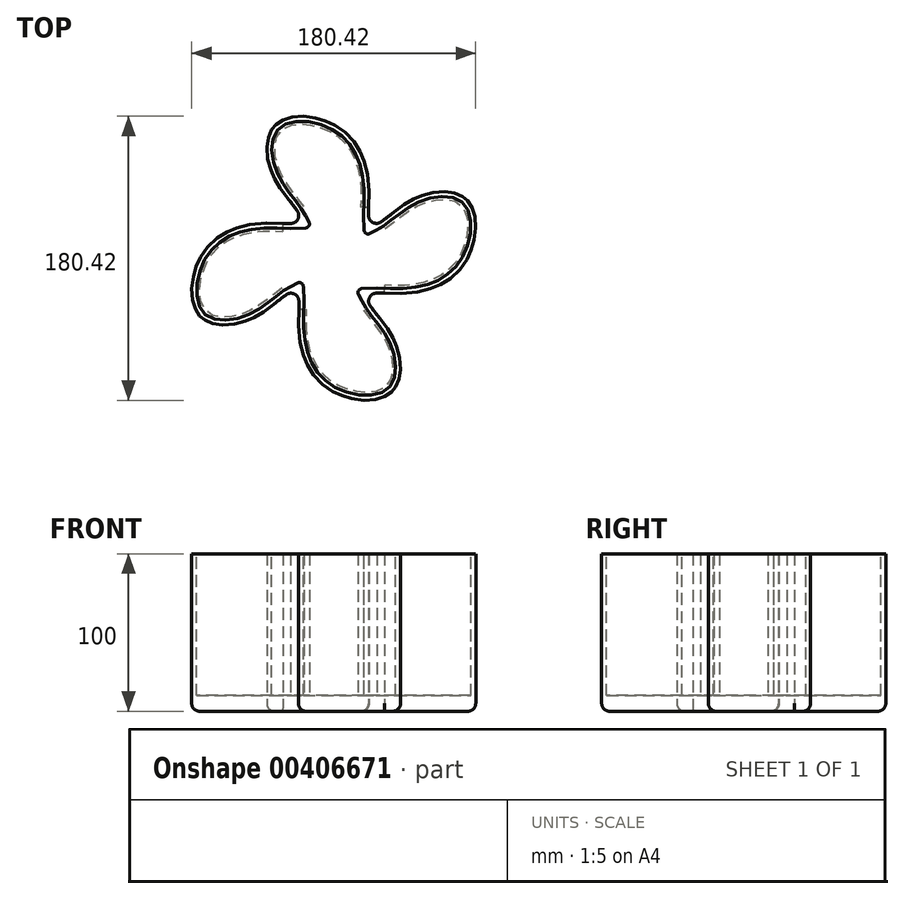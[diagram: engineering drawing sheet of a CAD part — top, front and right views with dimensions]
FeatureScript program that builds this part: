
annotation { "Feature Type Name" : "Feature", "Feature Type Description" : "" }
export const myFeature = defineFeature(function(context is Context, id is Id, definition is map)
    precondition{}
    {
        {
            var Q0;
            Q0=qCreatedBy(makeId("Top.planeOp"),FACE);
            var sketch = newSketch(context, id + "F0", { "sketchPlane" : qUnion([Q0])});
            skCircle(sketch, "E0", {"center": v(0, 0) * mm, "radius": 33.27 * mm, "construction": true});
            skFitSpline(sketch, "E1", {"points": [v(18.8, 27.45) * mm, v(15.3, 63.44) * mm, v(-5.91, 84.24) * mm, v(-35.04, 82.4) * mm, v(-36.55, 55.7) * mm, v(-21.57, 33.09) * mm, v(-14.6, 20.56) * mm], "startDerivative": vector(13.96, 201.86) * mm, "endDerivative": vector(40.78, -91.22) * mm});
            skLineSegment(sketch, "E2", {"start": v(-14.6, 20.56) * mm, "end": v(18.8, 27.45) * mm});
            skFitSpline(sketch, "E3.0", {"points": [v(21.79, 27.24) * mm, v(22.08, 31.5) * mm, v(22.45, 39.97) * mm, v(21.83, 50.18) * mm, v(20.34, 57.95) * mm, v(18.9, 62.61) * mm, v(17.41, 66.19) * mm, v(15.7, 69.63) * mm, v(13.11, 73.69) * mm, v(9.34, 78.06) * mm, v(4.92, 81.88) * mm, v(0.7, 84.54) * mm, v(-2.96, 86.31) * mm, v(-5.86, 87.46) * mm, v(-8.89, 88.42) * mm, v(-13.03, 89.42) * mm, v(-18.32, 90.14) * mm, v(-23.53, 90.07) * mm, v(-27.5, 89.45) * mm, v(-30.35, 88.67) * mm, v(-33.03, 87.56) * mm, v(-35.08, 86.3) * mm, v(-36.57, 85.1) * mm, v(-37.6, 84.08) * mm, v(-38.53, 82.98) * mm, v(-39.6, 81.4) * mm, v(-40.68, 79.29) * mm, v(-41.58, 76.57) * mm, v(-42.13, 73.73) * mm, v(-42.45, 69.8) * mm, v(-42.16, 64.76) * mm, v(-41.1, 59.74) * mm, v(-39.85, 55.86) * mm, v(-38.73, 53.05) * mm, v(-37.46, 50.4) * mm, v(-35.6, 47.05) * mm, v(-33.07, 43.18) * mm, v(-29.91, 38.98) * mm, v(-27.37, 35.78) * mm, v(-25.5, 33.38) * mm, v(-24.43, 31.95) * mm, v(-23.65, 30.83) * mm, v(-22.9, 29.73) * mm, v(-22.02, 28.37) * mm, v(-21.07, 26.78) * mm, v(-19.9, 24.7) * mm, v(-18.64, 22.19) * mm, v(-17.76, 20.27) * mm, v(-17.35, 19.33) * mm]});
            skLineSegment(sketch, "E4", {"start": v(-17.35, 19.33) * mm, "end": v(-14.6, 20.56) * mm});
            skLineSegment(sketch, "E5", {"start": v(18.8, 27.45) * mm, "end": v(22.14, 33.67) * mm});
            skLineSegment(sketch, "E6", {"start": v(22.14, 33.67) * mm, "end": v(22.14, 17.35) * mm});
            skLineSegment(sketch, "E7", {"start": v(22.14, 17.35) * mm, "end": v(19.33, 17.35) * mm});
            skLineSegment(sketch, "E8", {"start": v(19.33, 17.35) * mm, "end": v(18.8, 27.45) * mm});
            skPoint(sketch, "E9", {"position": v(0.24, 81.24) * mm});
            skSolve(sketch);
        }
        {
            var Q0;
            Q0=makeQuery(id+"F0.imprint","IMPRINT",FACE,{"disambiguationData":[TD([[makeQuery(id+"F0.imprint","IMPRINT",EDGE,{"derivedFrom":sQuery(id+"F0.wireOp",EDGE,"E1")}),-1.0]])]});
            var Q1;
            Q1=makeQuery(id+"F0.imprint","IMPRINT",FACE,{"disambiguationData":[TD([[makeQuery(id+"F0.imprint","IMPRINT",EDGE,{"derivedFrom":sQuery(id+"F0.wireOp",EDGE,"E5")}),-1.0]])]});
            extrude(context, id + "F1", {"entities" : qUnion([Q0, Q1]), "depth" : 100 * mm});
        }
        {
            var Q0;
            Q0=makeQuery(id+"F1.opExtrude","SWEPT_BODY",BODY,{"disambiguationData":[OSD([sQuery(id+"F0.wireOp",EDGE,"E1"),sQuery(id+"F0.wireOp",EDGE,"E3.0"),sQuery(id+"F0.wireOp",EDGE,"E4"),sQuery(id+"F0.wireOp",EDGE,"E5")])]});
            var Q1;
            Q1=sQuery(id+"F0.wireOp",EDGE,"E0");
            circularPattern(context, id + "F2", {"entities" : qUnion([Q0]), "axis" : qUnion([Q1]), "angle" : 360 * degree, "instanceCount" : 4, "equalSpace" : true});
        }
        {
            var Q0;
            Q0=makeQuery(id+"F1.opExtrude","SWEPT_BODY",BODY,{"disambiguationData":[OSD([sQuery(id+"F0.wireOp",EDGE,"E1"),sQuery(id+"F0.wireOp",EDGE,"E3.0"),sQuery(id+"F0.wireOp",EDGE,"E4"),sQuery(id+"F0.wireOp",EDGE,"E6"),sQuery(id+"F0.wireOp",EDGE,"E7"),sQuery(id+"F0.wireOp",EDGE,"E8")])]});
            var Q1;
            Q1=makeQuery(id+"F2.opPattern","COPY",BODY,{"derivedFrom":makeQuery(id+"F1.opExtrude","SWEPT_BODY",BODY,{"disambiguationData":[OSD([sQuery(id+"F0.wireOp",EDGE,"E1"),sQuery(id+"F0.wireOp",EDGE,"E3.0"),sQuery(id+"F0.wireOp",EDGE,"E4"),sQuery(id+"F0.wireOp",EDGE,"E6"),sQuery(id+"F0.wireOp",EDGE,"E7"),sQuery(id+"F0.wireOp",EDGE,"E8")])]}),"instanceName":"1"});
            var Q2;
            Q2=makeQuery(id+"F2.opPattern","COPY",BODY,{"derivedFrom":makeQuery(id+"F1.opExtrude","SWEPT_BODY",BODY,{"disambiguationData":[OSD([sQuery(id+"F0.wireOp",EDGE,"E1"),sQuery(id+"F0.wireOp",EDGE,"E3.0"),sQuery(id+"F0.wireOp",EDGE,"E4"),sQuery(id+"F0.wireOp",EDGE,"E6"),sQuery(id+"F0.wireOp",EDGE,"E7"),sQuery(id+"F0.wireOp",EDGE,"E8")])]}),"instanceName":"3"});
            booleanBodies(context, id + "F3", {"operationType" : BooleanOperationType.UNION, "tools" : qUnion([Q0, Q1, Q2])});
        }
        {
            var Q0;
            Q0=makeQuery(id+"F1.opExtrude","SWEPT_BODY",BODY,{"disambiguationData":[OSD([sQuery(id+"F0.wireOp",EDGE,"E1"),sQuery(id+"F0.wireOp",EDGE,"E3.0"),sQuery(id+"F0.wireOp",EDGE,"E4"),sQuery(id+"F0.wireOp",EDGE,"E6"),sQuery(id+"F0.wireOp",EDGE,"E7"),sQuery(id+"F0.wireOp",EDGE,"E8")])]});
            var Q1;
            Q1=makeQuery(id+"F2.opPattern","COPY",BODY,{"derivedFrom":makeQuery(id+"F1.opExtrude","SWEPT_BODY",BODY,{"disambiguationData":[OSD([sQuery(id+"F0.wireOp",EDGE,"E1"),sQuery(id+"F0.wireOp",EDGE,"E3.0"),sQuery(id+"F0.wireOp",EDGE,"E4"),sQuery(id+"F0.wireOp",EDGE,"E6"),sQuery(id+"F0.wireOp",EDGE,"E7"),sQuery(id+"F0.wireOp",EDGE,"E8")])]}),"instanceName":"2"});
            booleanBodies(context, id + "F4", {"operationType" : BooleanOperationType.UNION, "tools" : qUnion([Q0, Q1])});
        }
        {
            var Q0;
            Q0=makeQuery(id+"F4.opBoolean","INTERSECT",EDGE,{"derivedFrom":[makeQuery(id+"F2.opPattern","COPY",FACE,{"derivedFrom":makeQuery(id+"F1.opExtrude","SWEPT_FACE",FACE,{"disambiguationData":[OSD([sQuery(id+"F0.wireOp",EDGE,"E3.0")])]}),"instanceName":"1"}),makeQuery(id+"F2.opPattern","COPY",FACE,{"derivedFrom":makeQuery(id+"F1.opExtrude","SWEPT_FACE",FACE,{"disambiguationData":[OSD([sQuery(id+"F0.wireOp",EDGE,"E6")])]}),"instanceName":"2"})]});
            var Q1;
            Q1=makeQuery(id+"F4.opBoolean","INTERSECT",EDGE,{"derivedFrom":[makeQuery(id+"F2.opPattern","COPY",FACE,{"derivedFrom":makeQuery(id+"F1.opExtrude","SWEPT_FACE",FACE,{"disambiguationData":[OSD([sQuery(id+"F0.wireOp",EDGE,"E3.0")])]}),"instanceName":"2"}),makeQuery(id+"F2.opPattern","COPY",FACE,{"derivedFrom":makeQuery(id+"F1.opExtrude","SWEPT_FACE",FACE,{"disambiguationData":[OSD([sQuery(id+"F0.wireOp",EDGE,"E6")])]}),"instanceName":"3"})]});
            var Q2;
            Q2=makeQuery(id+"F3.opBoolean","INTERSECT",EDGE,{"derivedFrom":[makeQuery(id+"F1.opExtrude","SWEPT_FACE",FACE,{"disambiguationData":[OSD([sQuery(id+"F0.wireOp",EDGE,"E3.0")])]}),makeQuery(id+"F2.opPattern","COPY",FACE,{"derivedFrom":makeQuery(id+"F1.opExtrude","SWEPT_FACE",FACE,{"disambiguationData":[OSD([sQuery(id+"F0.wireOp",EDGE,"E6")])]}),"instanceName":"1"})]});
            var Q3;
            Q3=makeQuery(id+"F3.opBoolean","INTERSECT",EDGE,{"derivedFrom":[makeQuery(id+"F1.opExtrude","SWEPT_FACE",FACE,{"disambiguationData":[OSD([sQuery(id+"F0.wireOp",EDGE,"E6")])]}),makeQuery(id+"F2.opPattern","COPY",FACE,{"derivedFrom":makeQuery(id+"F1.opExtrude","SWEPT_FACE",FACE,{"disambiguationData":[OSD([sQuery(id+"F0.wireOp",EDGE,"E3.0")])]}),"instanceName":"3"})]});
            fillet(context, id + "F5", {"entities" : qUnion([Q0, Q1, Q2, Q3]), "radius" : 5 * mm, "tangentPropagation" : true, "allowEdgeOverflow" : false});
        }
        {
            var Q0;
            Q0=makeQuery(id+"F2.opPattern","COPY",EDGE,{"derivedFrom":makeQuery(id+"F1.opExtrude","SWEPT_EDGE",EDGE,{"disambiguationData":[OSD([sQuery(id+"F0.wireOp",EDGE,"E1"),sQuery(id+"F0.wireOp",EDGE,"E2"),sQuery(id+"F0.wireOp",EDGE,"E4")])]}),"instanceName":"2"});
            var Q1;
            Q1=makeQuery(id+"F4.opBoolean","INTERSECT",EDGE,{"derivedFrom":[makeQuery(id+"F2.opPattern","COPY",FACE,{"derivedFrom":makeQuery(id+"F1.opExtrude","SWEPT_FACE",FACE,{"disambiguationData":[OSD([sQuery(id+"F0.wireOp",EDGE,"E3.0")])]}),"instanceName":"2"}),makeQuery(id+"F2.opPattern","COPY",FACE,{"derivedFrom":makeQuery(id+"F1.opExtrude","SWEPT_FACE",FACE,{"disambiguationData":[OSD([sQuery(id+"F0.wireOp",EDGE,"E8")])]}),"instanceName":"3"})]});
            var Q2;
            Q2=makeQuery(id+"F2.opPattern","COPY",EDGE,{"derivedFrom":makeQuery(id+"F1.opExtrude","SWEPT_EDGE",EDGE,{"disambiguationData":[OSD([sQuery(id+"F0.wireOp",EDGE,"E1"),sQuery(id+"F0.wireOp",EDGE,"E2"),sQuery(id+"F0.wireOp",EDGE,"E4")])]}),"instanceName":"3"});
            var Q3;
            Q3=makeQuery(id+"F3.opBoolean","INTERSECT",EDGE,{"derivedFrom":[makeQuery(id+"F1.opExtrude","SWEPT_FACE",FACE,{"disambiguationData":[OSD([sQuery(id+"F0.wireOp",EDGE,"E8")])]}),makeQuery(id+"F2.opPattern","COPY",FACE,{"derivedFrom":makeQuery(id+"F1.opExtrude","SWEPT_FACE",FACE,{"disambiguationData":[OSD([sQuery(id+"F0.wireOp",EDGE,"E3.0")])]}),"instanceName":"3"})]});
            var Q4;
            Q4=makeQuery(id+"F2.opPattern","COPY",EDGE,{"derivedFrom":makeQuery(id+"F1.opExtrude","SWEPT_EDGE",EDGE,{"disambiguationData":[OSD([sQuery(id+"F0.wireOp",EDGE,"E1"),sQuery(id+"F0.wireOp",EDGE,"E2"),sQuery(id+"F0.wireOp",EDGE,"E4")])]}),"instanceName":"1"});
            var Q5;
            Q5=makeQuery(id+"F4.opBoolean","INTERSECT",EDGE,{"derivedFrom":[makeQuery(id+"F2.opPattern","COPY",FACE,{"derivedFrom":makeQuery(id+"F1.opExtrude","SWEPT_FACE",FACE,{"disambiguationData":[OSD([sQuery(id+"F0.wireOp",EDGE,"E3.0")])]}),"instanceName":"1"}),makeQuery(id+"F2.opPattern","COPY",FACE,{"derivedFrom":makeQuery(id+"F1.opExtrude","SWEPT_FACE",FACE,{"disambiguationData":[OSD([sQuery(id+"F0.wireOp",EDGE,"E8")])]}),"instanceName":"2"})]});
            var Q6;
            Q6=makeQuery(id+"F1.opExtrude","SWEPT_EDGE",EDGE,{"disambiguationData":[OSD([sQuery(id+"F0.wireOp",EDGE,"E1"),sQuery(id+"F0.wireOp",EDGE,"E2"),sQuery(id+"F0.wireOp",EDGE,"E4")])]});
            var Q7;
            Q7=makeQuery(id+"F3.opBoolean","INTERSECT",EDGE,{"derivedFrom":[makeQuery(id+"F1.opExtrude","SWEPT_FACE",FACE,{"disambiguationData":[OSD([sQuery(id+"F0.wireOp",EDGE,"E3.0")])]}),makeQuery(id+"F2.opPattern","COPY",FACE,{"derivedFrom":makeQuery(id+"F1.opExtrude","SWEPT_FACE",FACE,{"disambiguationData":[OSD([sQuery(id+"F0.wireOp",EDGE,"E8")])]}),"instanceName":"1"})]});
            fillet(context, id + "F6", {"entities" : qUnion([Q0, Q1, Q2, Q3, Q4, Q5, Q6, Q7]), "radius" : 2.5 * mm, "tangentPropagation" : true, "allowEdgeOverflow" : false});
        }
        {
            var Q0;
            Q0 = qSketchRegion(id + "F0", true);
            extrude(context, id + "F7", {"entities" : qUnion([Q0]), "operationType" : NewBodyOperationType.ADD, "depth" : 10 * mm});
        }
        {
            var Q0;
            Q0=makeQuery(id+"F1.opExtrude","SWEPT_BODY",BODY,{"disambiguationData":[OSD([sQuery(id+"F0.wireOp",EDGE,"E1"),sQuery(id+"F0.wireOp",EDGE,"E3.0"),sQuery(id+"F0.wireOp",EDGE,"E4"),sQuery(id+"F0.wireOp",EDGE,"E6"),sQuery(id+"F0.wireOp",EDGE,"E7"),sQuery(id+"F0.wireOp",EDGE,"E8")])]});
            var Q1;
            Q1=sQuery(id+"F0.wireOp",EDGE,"E0");
            circularPattern(context, id + "F8", {"entities" : qUnion([Q0]), "axis" : qUnion([Q1]), "angle" : 360 * degree, "instanceCount" : 4, "equalSpace" : true});
        }
        {
            var Q0;
            Q0=qCreatedBy(makeId("Top.planeOp"),FACE);
            var sketch = newSketch(context, id + "F9", { "sketchPlane" : qUnion([Q0])});
            skCircle(sketch, "E10", {"center": v(0, 0) * mm, "radius": 33.32 * mm});
            skSolve(sketch);
        }
        {
            var Q0;
            Q0 = qSketchRegion(id + "F9", true);
            extrude(context, id + "F10", {"entities" : qUnion([Q0]), "operationType" : NewBodyOperationType.ADD, "depth" : 10 * mm});
        }
        {
            var Q0;
            Q0=qCreatedBy(makeId("Right.planeOp"),FACE);
            var sketch = newSketch(context, id + "F11", { "sketchPlane" : qUnion([Q0])});
            skFitSpline(sketch, "E11", {"points": [v(-131.57, 50.31) * mm, v(-30.63, 93.43) * mm, v(35.07, 70.16) * mm, v(76.48, 54.76) * mm, v(142.86, 78.03) * mm, v(120.1, 125.02) * mm, v(44.22, 150.06) * mm, v(-154.5, 148.5) * mm, v(-196.75, 95.3) * mm, v(-131.57, 50.31) * mm]});
            skSolve(sketch);
        }
        {
            var Q0;
            {var subQ0=sQuery(id+"F0.wireOp",EDGE,"E8");var subQ1=sQuery(id+"F0.wireOp",EDGE,"E7");var subQ2=sQuery(id+"F0.wireOp",EDGE,"E6");var subQ3=sQuery(id+"F0.wireOp",EDGE,"E4");var subQ4=sQuery(id+"F0.wireOp",EDGE,"E3.0");var subQ5=makeQuery(id+"F1.opExtrude","CAP_FACE",FACE,{"disambiguationData":[OSD([sQuery(id+"F0.wireOp",EDGE,"E1"),subQ4,subQ3,subQ2,subQ1,subQ0])],"isStart":true});var subQ6=makeQuery(id+"F7.boolean.opBoolean","MERGE",FACE,{"derivedFrom":[makeQuery(id+"F4.opBoolean","MERGE",FACE,{"derivedFrom":[makeQuery(id+"F2.opPattern","COPY",FACE,{"derivedFrom":subQ5,"instanceName":"2"}),makeQuery(id+"F3.opBoolean","MERGE",FACE,{"derivedFrom":[subQ5,makeQuery(id+"F2.opPattern","COPY",FACE,{"derivedFrom":subQ5,"instanceName":"1"}),makeQuery(id+"F2.opPattern","COPY",FACE,{"derivedFrom":subQ5,"instanceName":"3"})]})]}),makeQuery(id+"F7.opExtrude","CAP_FACE",FACE,{"disambiguationData":[OSD([sQuery(id+"F0.wireOp",EDGE,"E2"),subQ4,subQ3,subQ2,subQ1,subQ0])],"isStart":true})]});Q0=makeQuery(id+"F10.boolean.opBoolean","MERGE",FACE,{"derivedFrom":[subQ6,makeQuery(id+"F8.opPattern","COPY",FACE,{"derivedFrom":subQ6,"instanceName":"1"}),makeQuery(id+"F8.opPattern","COPY",FACE,{"derivedFrom":subQ6,"instanceName":"2"}),makeQuery(id+"F8.opPattern","COPY",FACE,{"derivedFrom":subQ6,"instanceName":"3"}),makeQuery(id+"F10.opExtrude","CAP_FACE",FACE,{"disambiguationData":[OSD([sQuery(id+"F9.wireOp",EDGE,"E10")])],"isStart":true})]});}
            fillet(context, id + "F12", {"entities" : qUnion([Q0]), "radius" : 5 * mm, "tangentPropagation" : true, "allowEdgeOverflow" : false});
        }
    });
